# Revit family: Displays_Track_ASHanging_Contempo_WallTrack_Straight
name_source: partatom
category: Generic Models
units: mm (PartAtom-declared; Revit-internal decimal feet)

## family parameters
Can host rebar = No
Classification Number = 23.40.90.11
Cut with Voids When Loaded = No
Maintain Annotation Orientation = No
Part Type = Normal
Room Calculation Point = No
Round Connector Dimension = Use Diameter
Shared = No

## types (2) — shared parameters
Assembly Code = C1030500
Default Elevation = 0' - 0"
Description = AS Hanging Contempo Wall Track
Installation-Fabrication = https://www.ashanging.com
Keynote = 10 14 00
Manufacturer = AS Hanging
Manufacturer Website = https://www.ashanging.com
Model = Contempo Wall Track
Product Data = http://www.arcat.com
Product Properties = https://www.ashanging.com
Revision = R1_2017
Sales Information = https://www.ashanging.com
Specification = http://www.arcat.com
URL = https://www.ashanging.com

## per-type parameters (varying)
| type | Surface Finish |
| Silver Satin | Silver Satin |
| White | White Painted - Flat Finish |

## geometry (parser evidence)
native form markers: Sweep x5
no freeform markers — native parametric forms only
